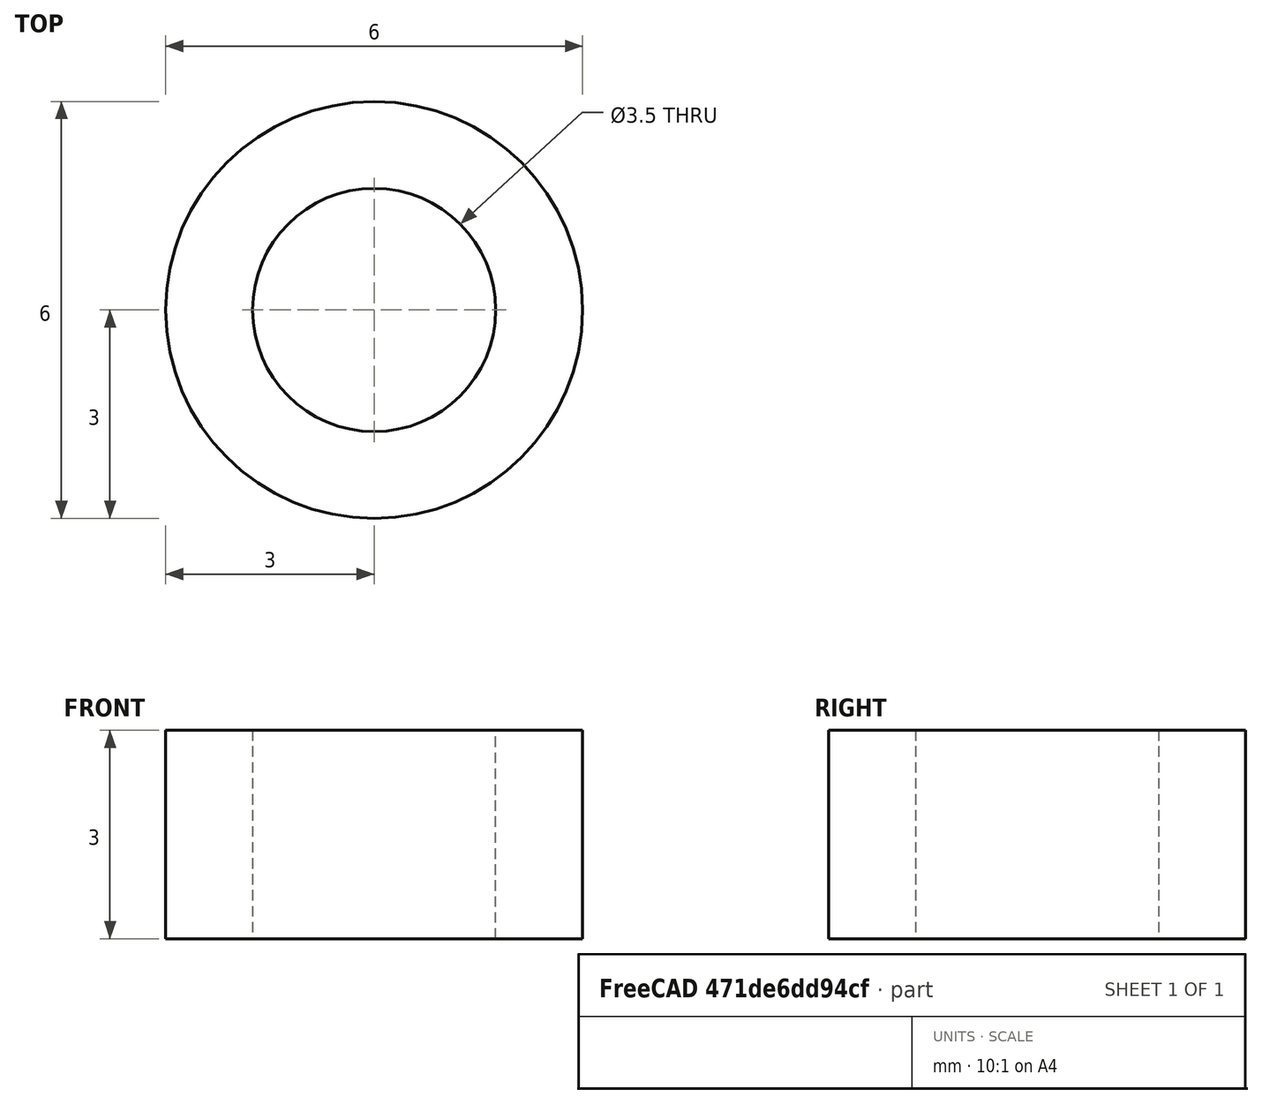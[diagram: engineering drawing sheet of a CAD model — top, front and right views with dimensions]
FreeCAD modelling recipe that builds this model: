
FCSTD DOCUMENT  (FreeCAD 0.21R33668 +26 (Git))
Label: separador 3mm
License: All rights reserved
LicenseURL: https://en.wikipedia.org/wiki/All_rights_reserved
objects: Sketcher::SketchObject×1, PartDesign::Pad×1, PartDesign::Body×1
note: 4 computed .brp shape members not serialized (recipe doc carries the construction recipe); baked Part::Feature solids carry a one-line shape summary decoded from their .brp

FEATURE [Sketcher::SketchObject] Sketch
  FullyConstrained = true
  MapMode = 5
  Support = -> [XY_Plane]
  sketch-geometry (2):
    g0: Circle CenterX=0 CenterY=0 CenterZ=0 NormalX=0 NormalY=0 NormalZ=1 AngleXU=0 Radius=1.75
    g1: Circle CenterX=0 CenterY=0 CenterZ=0 NormalX=0 NormalY=0 NormalZ=1 AngleXU=0 Radius=3
  constraints (4):
    c: Coincident(g0,g-1)
    c: Coincident(g1,g0)
    c: Diameter(g0) = 3.5
    c: Diameter(g1) = 6
FEATURE [PartDesign::Pad] Pad
  Direction = (0,0,1)
  Length = 3
  Length2 = 10
  Profile = -> Sketch
  ReferenceAxis = -> Sketch [N_Axis]
  Type = 0
FEATURE [PartDesign::Body] Body  label="Cuerpo"
  Group = -> [Sketch,Pad]
  Origin = -> Origin
  Tip = -> Pad
